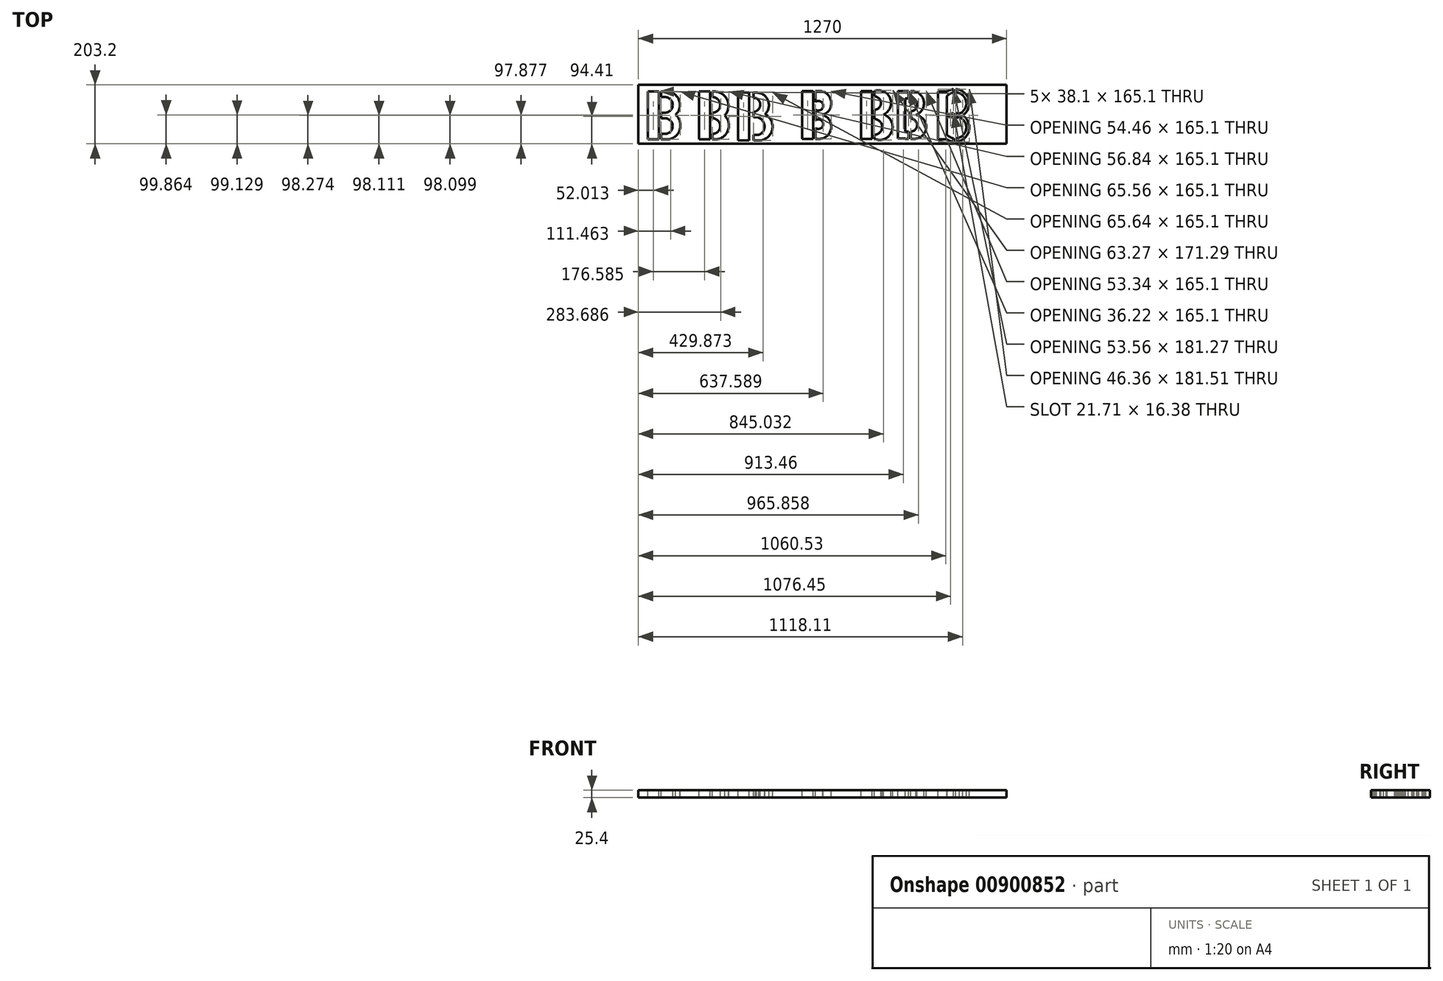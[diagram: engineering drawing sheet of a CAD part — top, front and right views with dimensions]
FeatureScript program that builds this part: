
annotation { "Feature Type Name" : "Feature", "Feature Type Description" : "" }
export const myFeature = defineFeature(function(context is Context, id is Id, definition is map)
    precondition{}
    {
        {
            var Q0;
            Q0=qCreatedBy(makeId("Top.planeOp"),FACE);
            var sketch = newSketch(context, id + "F0", { "sketchPlane" : qUnion([Q0])});
            skLineSegment(sketch, "E0.bottom", {"start": v(-873.94, -930.87) * mm, "end": v(396.06, -930.87) * mm});
            skLineSegment(sketch, "E0.top", {"start": v(-873.94, -1134.07) * mm, "end": v(396.06, -1134.07) * mm});
            skLineSegment(sketch, "E0.left", {"start": v(-873.94, -930.87) * mm, "end": v(-873.94, -1134.07) * mm});
            skLineSegment(sketch, "E0.right", {"start": v(396.06, -930.87) * mm, "end": v(396.06, -1134.07) * mm});
            skSolve(sketch);
        }
        {
            var Q0;
            Q0=makeQuery(id+"F0.imprint","IMPRINT",FACE,{"disambiguationData":[TD([[makeQuery(id+"F0.imprint","IMPRINT",EDGE,{"derivedFrom":sQuery(id+"F0.wireOp",EDGE,"E0.bottom")}),-1.0]])]});
            extrude(context, id + "F1", {"entities" : qUnion([Q0]), "depth" : 25.4 * mm, "offsetDistance" : 25.4 * mm});
        }
        {
            var Q0;
            Q0=makeQuery(id+"F1.opExtrude","CAP_FACE",FACE,{"disambiguationData":[OSD([sQuery(id+"F0.wireOp",EDGE,"E0.bottom"),sQuery(id+"F0.wireOp",EDGE,"E0.top"),sQuery(id+"F0.wireOp",EDGE,"E0.left"),sQuery(id+"F0.wireOp",EDGE,"E0.right")])],"isStart":false});
            var sketch = newSketch(context, id + "F2", { "sketchPlane" : qUnion([Q0])});
            skLineSegment(sketch, "E1.bottom", {"start": v(-840.98, -953.64) * mm, "end": v(-802.88, -953.64) * mm});
            skLineSegment(sketch, "E1.top", {"start": v(-840.98, -1118.74) * mm, "end": v(-802.88, -1118.74) * mm});
            skLineSegment(sketch, "E1.left", {"start": v(-840.98, -953.64) * mm, "end": v(-840.98, -1118.74) * mm});
            skLineSegment(sketch, "E1.right", {"start": v(-802.88, -953.64) * mm, "end": v(-802.88, -1118.74) * mm});
            skLineSegment(sketch, "E2", {"start": v(-795.26, -953.64) * mm, "end": v(-795.26, -1118.74) * mm});
            skLineSegment(sketch, "E3", {"start": v(-795.26, -953.64) * mm, "end": v(-776.2, -953.64) * mm});
            skPoint(sketch, "E3.endSnap0", {"position": v(-776.2, -1036.2) * mm});
            skLineSegment(sketch, "E4", {"start": v(-795.26, -1118.74) * mm, "end": v(-776.2, -1118.74) * mm});
            skLineSegment(sketch, "E5", {"start": v(-795.26, -1026.67) * mm, "end": v(-782.56, -1026.67) * mm});
            skLineSegment(sketch, "E6", {"start": v(-795.26, -1045.72) * mm, "end": v(-782.56, -1045.72) * mm});
            skLineSegment(sketch, "E7", {"start": v(-795.26, -1099.7) * mm, "end": v(-782.56, -1099.7) * mm});
            skArc(sketch, "E8", {"start": v(-782.56, -1099.7) * mm, "mid": v(-755.57, -1072.7) * mm, "end": v(-782.56, -1045.72) * mm});
            skLineSegment(sketch, "E9", {"start": v(-795.26, -972.7) * mm, "end": v(-782.56, -972.7) * mm});
            skArc(sketch, "E10", {"start": v(-782.56, -1026.67) * mm, "mid": v(-755.57, -999.68) * mm, "end": v(-782.56, -972.7) * mm});
            skLineSegment(sketch, "E11", {"start": v(-729.7, -1066.36) * mm, "end": v(-729.7, -1079.06) * mm});
            skPoint(sketch, "E12.orphan", {"position": v(-802.96, -1036.2) * mm});
            skLineSegment(sketch, "E13", {"start": v(-795.26, -1036.2) * mm, "end": v(-807.9, -1036.2) * mm});
            skLineSegment(sketch, "E14", {"start": v(-731.4, -993.33) * mm, "end": v(-731.4, -1006.03) * mm});
            skArc(sketch, "E15", {"start": v(-731.4, -993.33) * mm, "mid": v(-746.28, -965) * mm, "end": v(-776.2, -953.64) * mm});
            skArc(sketch, "E16", {"start": v(-729.7, -1066.36) * mm, "mid": v(-753.48, -1029.59) * mm, "end": v(-796.76, -1036.2) * mm});
            skArc(sketch, "E17", {"start": v(-776.2, -1118.74) * mm, "mid": v(-745.64, -1107.47) * mm, "end": v(-729.7, -1079.06) * mm});
            skArc(sketch, "E18.trimOffspring", {"start": v(-796.76, -1036.2) * mm, "mid": v(-755.37, -1039.98) * mm, "end": v(-731.4, -1006.03) * mm});
            skSolve(sketch);
        }
        {
            var Q0;
            Q0=makeQuery(id+"F2.imprint","IMPRINT",FACE,{"disambiguationData":[TD([[makeQuery(id+"F2.imprint","IMPRINT",EDGE,{"derivedFrom":sQuery(id+"F2.wireOp",EDGE,"E1.bottom")}),-1.0]])]});
            var Q1;
            {var subQ0=sQuery(id+"F2.wireOp",EDGE,"idpBYQ9l-Ms9j-yzLq-ZXLM-ZtzVa5Vgj7Lw");Q1=makeQuery(id+"F2.imprint","IMPRINT",FACE,{"disambiguationData":[TD([[makeQuery(id+"F2.imprint","IMPRINT",EDGE,{"derivedFrom":subQ0}),1.0]])]});}
            var Q2;
            {var subQ1=sQuery(id+"F2.wireOp",EDGE,"idpBYQ9l-Ms9j-yzLq-ZXLM-ZtzVa5Vgj7Lw");Q2=makeQuery(id+"F2.imprint","IMPRINT",FACE,{"disambiguationData":[TD([[makeQuery(id+"F2.imprint","IMPRINT",EDGE,{"derivedFrom":subQ1}),-1.0]])]});}
            var Q3;
            {var subQ5=sQuery(id+"F2.wireOp",EDGE,"E3");Q3=makeQuery(id+"F2.imprint","IMPRINT",FACE,{"disambiguationData":[TD([[makeQuery(id+"F2.imprint","IMPRINT",EDGE,{"derivedFrom":subQ5}),-1.0]])]});}
            var Q4;
            {var subQ1=sQuery(id+"F2.wireOp",EDGE,"E4");Q4=makeQuery(id+"F2.imprint","IMPRINT",FACE,{"disambiguationData":[TD([[makeQuery(id+"F2.imprint","IMPRINT",EDGE,{"derivedFrom":subQ1}),1.0]])]});}
            var Q5;
            {var subQ0=sQuery(id+"F2.wireOp",EDGE,"E2");var subQ1=makeQuery(id+"F2.imprint","INTERSECT",VERTEX,{"derivedFrom":[subQ0,sQuery(id+"F2.wireOp",EDGE,"E13")]});Q5=makeQuery(id+"F2.imprint","IMPRINT",FACE,{"disambiguationData":[TD([[makeQuery(id+"F2.imprint","IMPRINT",EDGE,{"disambiguationData":[TD([[subQ1,1.0]])],"derivedFrom":subQ0}),1.0]])]});}
            extrude(context, id + "F3", {"entities" : qUnion([Q0, Q1, Q2, Q3, Q4, Q5]), "operationType" : NewBodyOperationType.REMOVE, "oppositeDirection" : true, "depth" : 25.4 * mm, "offsetDistance" : 25.4 * mm});
        }
        {
            var Q0;
            Q0=makeQuery(id+"F1.opExtrude","CAP_FACE",FACE,{"disambiguationData":[OSD([sQuery(id+"F0.wireOp",EDGE,"E0.bottom"),sQuery(id+"F0.wireOp",EDGE,"E0.top"),sQuery(id+"F0.wireOp",EDGE,"E0.left"),sQuery(id+"F0.wireOp",EDGE,"E0.right")])],"isStart":false});
            var sketch = newSketch(context, id + "F4", { "sketchPlane" : qUnion([Q0])});
            skLineSegment(sketch, "E19.bottom", {"start": v(-664.4, -953.64) * mm, "end": v(-626.3, -953.64) * mm});
            skLineSegment(sketch, "E19.top", {"start": v(-664.4, -1118.74) * mm, "end": v(-626.3, -1118.74) * mm});
            skLineSegment(sketch, "E19.left", {"start": v(-664.4, -953.64) * mm, "end": v(-664.4, -1118.74) * mm});
            skLineSegment(sketch, "E19.right", {"start": v(-626.3, -953.64) * mm, "end": v(-626.3, -1118.74) * mm});
            skLineSegment(sketch, "E20", {"start": v(-661.28, -1036.2) * mm, "end": v(-576.47, -1036.2) * mm});
            skLineSegment(sketch, "E21", {"start": v(-618.67, -953.64) * mm, "end": v(-618.67, -1118.74) * mm});
            skLineSegment(sketch, "E22", {"start": v(-618.67, -953.64) * mm, "end": v(-612.21, -953.64) * mm});
            skLineSegment(sketch, "E23", {"start": v(-618.67, -972.7) * mm, "end": v(-610.9, -972.7) * mm});
            skLineSegment(sketch, "E24", {"start": v(-618.67, -1026.67) * mm, "end": v(-596.99, -1026.67) * mm});
            skLineSegment(sketch, "E25", {"start": v(-618.67, -1045.72) * mm, "end": v(-598.32, -1045.72) * mm});
            skLineSegment(sketch, "E26", {"start": v(-618.67, -1118.74) * mm, "end": v(-609.58, -1118.74) * mm});
            skLineSegment(sketch, "E27", {"start": v(-618.67, -1099.7) * mm, "end": v(-610.24, -1099.7) * mm});
            skArc(sketch, "E28", {"start": v(-618.67, -1026.67) * mm, "mid": v(-591.69, -999.68) * mm, "end": v(-618.67, -972.7) * mm});
            skArc(sketch, "E29", {"start": v(-618.67, -1099.7) * mm, "mid": v(-591.69, -1072.7) * mm, "end": v(-618.67, -1045.72) * mm});
            skArc(sketch, "E30", {"start": v(-609.58, -1118.74) * mm, "mid": v(-565.11, -1088.67) * mm, "end": v(-576.47, -1036.2) * mm});
            skArc(sketch, "E31", {"start": v(-576.47, -1036.2) * mm, "mid": v(-567.23, -983.18) * mm, "end": v(-612.21, -953.64) * mm});
            skSolve(sketch);
        }
        {
            var Q0;
            {var subQ1=sQuery(id+"F4.wireOp",EDGE,"E19.bottom");Q0=makeQuery(id+"F4.imprint","IMPRINT",FACE,{"disambiguationData":[TD([[makeQuery(id+"F4.imprint","IMPRINT",EDGE,{"derivedFrom":subQ1}),-1.0]])]});}
            var Q1;
            {var subQ0=sQuery(id+"F4.wireOp",EDGE,"E22");Q1=makeQuery(id+"F4.imprint","IMPRINT",FACE,{"disambiguationData":[TD([[makeQuery(id+"F4.imprint","IMPRINT",EDGE,{"derivedFrom":subQ0}),-1.0]])]});}
            var Q2;
            {var subQ0=sQuery(id+"F4.wireOp",EDGE,"E26");Q2=makeQuery(id+"F4.imprint","IMPRINT",FACE,{"disambiguationData":[TD([[makeQuery(id+"F4.imprint","IMPRINT",EDGE,{"derivedFrom":subQ0}),1.0]])]});}
            extrude(context, id + "F5", {"entities" : qUnion([Q0, Q1, Q2]), "operationType" : NewBodyOperationType.REMOVE, "oppositeDirection" : true, "depth" : 25.4 * mm, "offsetDistance" : 25.4 * mm});
        }
        {
            var Q0;
            Q0=makeQuery(id+"F1.opExtrude","CAP_FACE",FACE,{"disambiguationData":[OSD([sQuery(id+"F0.wireOp",EDGE,"E0.bottom"),sQuery(id+"F0.wireOp",EDGE,"E0.top"),sQuery(id+"F0.wireOp",EDGE,"E0.left"),sQuery(id+"F0.wireOp",EDGE,"E0.right")])],"isStart":false});
            var sketch = newSketch(context, id + "F6", { "sketchPlane" : qUnion([Q0])});
            skLineSegment(sketch, "E32.bottom", {"start": v(-309.3, -951.66) * mm, "end": v(-271.2, -951.66) * mm});
            skLineSegment(sketch, "E32.top", {"start": v(-309.3, -1116.76) * mm, "end": v(-271.2, -1116.76) * mm});
            skLineSegment(sketch, "E32.left", {"start": v(-309.3, -951.66) * mm, "end": v(-309.3, -1116.76) * mm});
            skLineSegment(sketch, "E32.right", {"start": v(-271.2, -951.66) * mm, "end": v(-271.2, -1116.76) * mm});
            skLineSegment(sketch, "E33", {"start": v(-263.58, -951.66) * mm, "end": v(-263.58, -1116.76) * mm});
            skLineSegment(sketch, "E34", {"start": v(-263.58, -951.66) * mm, "end": v(-250.88, -951.66) * mm});
            skLineSegment(sketch, "E35", {"start": v(-263.58, -1034.2) * mm, "end": v(-238.18, -1034.2) * mm});
            skLineSegment(sketch, "E36", {"start": v(-263.58, -1116.76) * mm, "end": v(-250.88, -1116.76) * mm});
            skLineSegment(sketch, "E37", {"start": v(-263.58, -1015.16) * mm, "end": v(-234.08, -1015.16) * mm});
            skLineSegment(sketch, "E38", {"start": v(-263.58, -1053.26) * mm, "end": v(-237.49, -1053.26) * mm});
            skLineSegment(sketch, "E39", {"start": v(-263.58, -989.76) * mm, "end": v(-228.48, -989.76) * mm});
            skLineSegment(sketch, "E40", {"start": v(-263.58, -1078.66) * mm, "end": v(-221.73, -1078.66) * mm});
            skArc(sketch, "E41", {"start": v(-263.58, -1015.16) * mm, "mid": v(-236.52, -1002.46) * mm, "end": v(-263.58, -989.76) * mm});
            skArc(sketch, "E42", {"start": v(-263.58, -1078.66) * mm, "mid": v(-236.52, -1065.96) * mm, "end": v(-263.58, -1053.26) * mm});
            skArc(sketch, "E43", {"start": v(-238.18, -1034.2) * mm, "mid": v(-209.12, -987.48) * mm, "end": v(-250.88, -951.66) * mm});
            skArc(sketch, "E44", {"start": v(-250.88, -1116.76) * mm, "mid": v(-209.12, -1080.93) * mm, "end": v(-238.18, -1034.2) * mm});
            skSolve(sketch);
        }
        {
            var Q0;
            Q0=makeQuery(id+"F6.imprint","IMPRINT",FACE,{"disambiguationData":[TD([[makeQuery(id+"F6.imprint","IMPRINT",EDGE,{"derivedFrom":sQuery(id+"F6.wireOp",EDGE,"E32.bottom")}),-1.0]])]});
            var Q1;
            {var subQ0=sQuery(id+"F6.wireOp",EDGE,"E34");Q1=makeQuery(id+"F6.imprint","IMPRINT",FACE,{"disambiguationData":[TD([[makeQuery(id+"F6.imprint","IMPRINT",EDGE,{"derivedFrom":subQ0}),-1.0]])]});}
            var Q2;
            {var subQ0=sQuery(id+"F6.wireOp",EDGE,"E35");Q2=makeQuery(id+"F6.imprint","IMPRINT",FACE,{"disambiguationData":[TD([[makeQuery(id+"F6.imprint","IMPRINT",EDGE,{"derivedFrom":subQ0}),-1.0]])]});}
            extrude(context, id + "F7", {"entities" : qUnion([Q0, Q1, Q2]), "operationType" : NewBodyOperationType.REMOVE, "oppositeDirection" : true, "depth" : 25.4 * mm, "offsetDistance" : 25.4 * mm});
        }
        {
            var Q0;
            Q0=makeQuery(id+"F1.opExtrude","CAP_FACE",FACE,{"disambiguationData":[OSD([sQuery(id+"F0.wireOp",EDGE,"E0.bottom"),sQuery(id+"F0.wireOp",EDGE,"E0.top"),sQuery(id+"F0.wireOp",EDGE,"E0.left"),sQuery(id+"F0.wireOp",EDGE,"E0.right")])],"isStart":false});
            var sketch = newSketch(context, id + "F8", { "sketchPlane" : qUnion([Q0])});
            skLineSegment(sketch, "E45", {"start": v(-530.23, -957.11) * mm, "end": v(-530.23, -1122.21) * mm});
            skLineSegment(sketch, "E46", {"start": v(-530.23, -1122.21) * mm, "end": v(-492.13, -1122.21) * mm});
            skLineSegment(sketch, "E47", {"start": v(-492.13, -1122.21) * mm, "end": v(-492.13, -957.11) * mm});
            skLineSegment(sketch, "E48", {"start": v(-492.13, -957.11) * mm, "end": v(-530.23, -957.11) * mm});
            skLineSegment(sketch, "E49", {"start": v(-476.9, -1122.21) * mm, "end": v(-458.66, -1122.21) * mm});
            skLineSegment(sketch, "E50", {"start": v(-476.9, -1103.16) * mm, "end": v(-458.66, -1103.16) * mm});
            skLineSegment(sketch, "E51", {"start": v(-458.66, -1103.16) * mm, "end": v(-458.66, -1103.94) * mm});
            skLineSegment(sketch, "E52", {"start": v(-476.9, -1041.57) * mm, "end": v(-470.78, -1041.57) * mm});
            skLineSegment(sketch, "E53", {"start": v(-476.9, -1022.52) * mm, "end": v(-470.78, -1022.52) * mm});
            skLineSegment(sketch, "E54", {"start": v(-476.9, -957.11) * mm, "end": v(-467.16, -957.11) * mm});
            skLineSegment(sketch, "E55", {"start": v(-476.9, -976.16) * mm, "end": v(-467.16, -976.16) * mm});
            skArc(sketch, "E56", {"start": v(-470.78, -1022.52) * mm, "mid": v(-453.83, -1000.52) * mm, "end": v(-467.16, -976.16) * mm});
            skArc(sketch, "E57", {"start": v(-437.13, -1032.04) * mm, "mid": v(-426.8, -984.42) * mm, "end": v(-467.16, -957.11) * mm});
            skArc(sketch, "E58", {"start": v(-458.66, -1122.21) * mm, "mid": v(-412.31, -1085.62) * mm, "end": v(-437.13, -1032.04) * mm});
            skArc(sketch, "E59", {"start": v(-458.66, -1103.16) * mm, "mid": v(-439.4, -1067.38) * mm, "end": v(-470.78, -1041.57) * mm});
            skLineSegment(sketch, "E60", {"start": v(-476.9, -957.11) * mm, "end": v(-476.9, -1122.21) * mm});
            skSolve(sketch);
        }
        {
            var Q0;
            Q0=makeQuery(id+"F8.imprint","IMPRINT",FACE,{"disambiguationData":[TD([[makeQuery(id+"F8.imprint","IMPRINT",EDGE,{"derivedFrom":sQuery(id+"F8.wireOp",EDGE,"E45")}),1.0]])]});
            var Q1;
            {var subQ2=sQuery(id+"F8.wireOp",EDGE,"E49");Q1=makeQuery(id+"F8.imprint","IMPRINT",FACE,{"disambiguationData":[TD([[makeQuery(id+"F8.imprint","IMPRINT",EDGE,{"derivedFrom":subQ2}),1.0]])]});}
            extrude(context, id + "F9", {"entities" : qUnion([Q0, Q1]), "operationType" : NewBodyOperationType.REMOVE, "oppositeDirection" : true, "depth" : 25.4 * mm, "offsetDistance" : 25.4 * mm});
        }
        {
            var Q0;
            Q0=makeQuery(id+"F1.opExtrude","CAP_FACE",FACE,{"disambiguationData":[OSD([sQuery(id+"F0.wireOp",EDGE,"E0.bottom"),sQuery(id+"F0.wireOp",EDGE,"E0.top"),sQuery(id+"F0.wireOp",EDGE,"E0.left"),sQuery(id+"F0.wireOp",EDGE,"E0.right")])],"isStart":false});
            var sketch = newSketch(context, id + "F10", { "sketchPlane" : qUnion([Q0])});
            skLineSegment(sketch, "E61", {"start": v(-60.54, -951.66) * mm, "end": v(-60.54, -1116.76) * mm});
            skPoint(sketch, "E61.endSnap0", {"position": v(-290.25, -1116.76) * mm});
            skArc(sketch, "E62", {"start": v(-28.11, -1032.68) * mm, "mid": v(-5.68, -976.7) * mm, "end": v(-60.54, -951.66) * mm});
            skArc(sketch, "E63", {"start": v(-60.54, -1116.76) * mm, "mid": v(-0.26, -1091.71) * mm, "end": v(-28.11, -1032.68) * mm});
            skArc(sketch, "E64", {"start": v(-60.54, -1016.52) * mm, "mid": v(-37.36, -993.33) * mm, "end": v(-60.54, -970.14) * mm});
            skArc(sketch, "E65", {"start": v(-60.54, -1102.78) * mm, "mid": v(-33.24, -1075.48) * mm, "end": v(-60.54, -1048.18) * mm});
            skPoint(sketch, "E66.orphan", {"position": v(-60.54, -1034.2) * mm});
            skLineSegment(sketch, "E67.bottom", {"start": v(-106.26, -951.66) * mm, "end": v(-68.16, -951.66) * mm});
            skLineSegment(sketch, "E67.top", {"start": v(-106.26, -1116.76) * mm, "end": v(-68.16, -1116.76) * mm});
            skLineSegment(sketch, "E67.left", {"start": v(-106.26, -951.66) * mm, "end": v(-106.26, -1116.76) * mm});
            skLineSegment(sketch, "E67.right", {"start": v(-68.16, -951.66) * mm, "end": v(-68.16, -1116.76) * mm});
            skSolve(sketch);
        }
        {
            var Q0;
            {var subQ4=sQuery(id+"F10.wireOp",EDGE,"E62");Q0=makeQuery(id+"F10.imprint","IMPRINT",FACE,{"disambiguationData":[TD([[makeQuery(id+"F10.imprint","IMPRINT",EDGE,{"derivedFrom":subQ4}),1.0]])]});}
            var Q1;
            Q1=makeQuery(id+"F10.imprint","IMPRINT",FACE,{"disambiguationData":[TD([[makeQuery(id+"F10.imprint","IMPRINT",EDGE,{"derivedFrom":sQuery(id+"F10.wireOp",EDGE,"E67.bottom")}),-1.0]])]});
            extrude(context, id + "F11", {"entities" : qUnion([Q0, Q1]), "operationType" : NewBodyOperationType.REMOVE, "oppositeDirection" : true, "depth" : 25.4 * mm, "offsetDistance" : 25.4 * mm});
        }
        {
            var Q0;
            Q0=makeQuery(id+"F1.opExtrude","CAP_FACE",FACE,{"disambiguationData":[OSD([sQuery(id+"F0.wireOp",EDGE,"E0.bottom"),sQuery(id+"F0.wireOp",EDGE,"E0.top"),sQuery(id+"F0.wireOp",EDGE,"E0.left"),sQuery(id+"F0.wireOp",EDGE,"E0.right")])],"isStart":false});
            var sketch = newSketch(context, id + "F12", { "sketchPlane" : qUnion([Q0])});
            skLineSegment(sketch, "E68", {"start": v(46.81, -951.66) * mm, "end": v(46.81, -1116.76) * mm});
            skLineSegment(sketch, "E69", {"start": v(46.81, -1116.76) * mm, "end": v(57.63, -1116.76) * mm});
            skLineSegment(sketch, "E70", {"start": v(46.81, -951.66) * mm, "end": v(57.63, -951.66) * mm});
            skLineSegment(sketch, "E71", {"start": v(46.81, -1034.2) * mm, "end": v(57.63, -1034.2) * mm});
            skLineSegment(sketch, "E72", {"start": v(46.81, -977.06) * mm, "end": v(57.63, -977.06) * mm});
            skLineSegment(sketch, "E73", {"start": v(46.81, -1021.5) * mm, "end": v(57.63, -1021.5) * mm});
            skLineSegment(sketch, "E74", {"start": v(46.81, -1046.9) * mm, "end": v(57.63, -1046.9) * mm});
            skLineSegment(sketch, "E75", {"start": v(46.81, -1091.36) * mm, "end": v(57.63, -1091.36) * mm});
            skArc(sketch, "E76", {"start": v(65.25, -1021.5) * mm, "mid": v(87.47, -999.28) * mm, "end": v(65.25, -977.06) * mm});
            skArc(sketch, "E77", {"start": v(65.25, -1091.36) * mm, "mid": v(87.47, -1069.13) * mm, "end": v(65.25, -1046.9) * mm});
            skLineSegment(sketch, "E78.bottom", {"start": v(46.81, -951.66) * mm, "end": v(21.41, -951.66) * mm});
            skLineSegment(sketch, "E78.top", {"start": v(46.81, -1116.28) * mm, "end": v(21.41, -1116.28) * mm});
            skLineSegment(sketch, "E78.left", {"start": v(46.81, -951.66) * mm, "end": v(46.81, -1116.28) * mm});
            skLineSegment(sketch, "E78.right", {"start": v(21.41, -951.66) * mm, "end": v(21.41, -1116.28) * mm});
            skArc(sketch, "E79", {"start": v(83.54, -1034.2) * mm, "mid": v(110.4, -986.64) * mm, "end": v(68.45, -951.66) * mm});
            skArc(sketch, "E80", {"start": v(77.2, -1116.76) * mm, "mid": v(118.59, -1078.42) * mm, "end": v(83.54, -1034.2) * mm});
            skLineSegment(sketch, "E81.left", {"start": v(57.63, -951.66) * mm, "end": v(57.63, -1116.76) * mm});
            skLineSegment(sketch, "E81.right", {"start": v(65.25, -951.66) * mm, "end": v(65.25, -1116.76) * mm});
            skLineSegment(sketch, "E82.trimOffspring", {"start": v(65.25, -951.66) * mm, "end": v(68.45, -951.66) * mm});
            skLineSegment(sketch, "E83.trimOffspring", {"start": v(65.25, -1034.2) * mm, "end": v(83.54, -1034.2) * mm});
            skLineSegment(sketch, "E84.trimOffspring", {"start": v(65.25, -1116.76) * mm, "end": v(77.2, -1116.76) * mm});
            skPoint(sketch, "E81.top.end.orphan", {"position": v(65.25, -1125.77) * mm});
            skSolve(sketch);
        }
        {
            var Q0;
            {var subQ3=sQuery(id+"F12.wireOp",EDGE,"E78.bottom");Q0=makeQuery(id+"F12.imprint","IMPRINT",FACE,{"disambiguationData":[TD([[makeQuery(id+"F12.imprint","IMPRINT",EDGE,{"derivedFrom":subQ3}),1.0]])]});}
            var Q1;
            {var subQ4=sQuery(id+"F12.wireOp",EDGE,"E70");Q1=makeQuery(id+"F12.imprint","IMPRINT",FACE,{"disambiguationData":[TD([[makeQuery(id+"F12.imprint","IMPRINT",EDGE,{"derivedFrom":subQ4}),-1.0]])]});}
            var Q2;
            {var subQ3=sQuery(id+"F12.wireOp",EDGE,"E68");Q2=makeQuery(id+"F12.imprint","IMPRINT",FACE,{"disambiguationData":[TD([[makeQuery(id+"F12.imprint","IMPRINT",EDGE,{"derivedFrom":subQ3}),1.0]])]});}
            var Q3;
            {var subQ1=sQuery(id+"F12.wireOp",EDGE,"E76");Q3=makeQuery(id+"F12.imprint","IMPRINT",FACE,{"disambiguationData":[TD([[makeQuery(id+"F12.imprint","IMPRINT",EDGE,{"derivedFrom":subQ1}),-1.0]])]});}
            var Q4;
            {var subQ1=sQuery(id+"F12.wireOp",EDGE,"E77");Q4=makeQuery(id+"F12.imprint","IMPRINT",FACE,{"disambiguationData":[TD([[makeQuery(id+"F12.imprint","IMPRINT",EDGE,{"derivedFrom":subQ1}),-1.0]])]});}
            extrude(context, id + "F13", {"entities" : qUnion([Q0, Q1, Q2, Q3, Q4]), "operationType" : NewBodyOperationType.REMOVE, "oppositeDirection" : true, "depth" : 25.4 * mm, "offsetDistance" : 25.4 * mm});
        }
        {
            var Q0;
            Q0=makeQuery(id+"F1.opExtrude","CAP_FACE",FACE,{"disambiguationData":[OSD([sQuery(id+"F0.wireOp",EDGE,"E0.bottom"),sQuery(id+"F0.wireOp",EDGE,"E0.top"),sQuery(id+"F0.wireOp",EDGE,"E0.left"),sQuery(id+"F0.wireOp",EDGE,"E0.right")])],"isStart":false});
            var sketch = newSketch(context, id + "F14", { "sketchPlane" : qUnion([Q0])});
            skArc(sketch, "E85", {"start": v(191.66, -1036.74) * mm, "mid": v(202.1, -1041.64) * mm, "end": v(213.37, -1043.99) * mm});
            skArc(sketch, "E86", {"start": v(190.37, -1118.46) * mm, "mid": v(201.36, -1123.97) * mm, "end": v(213.37, -1126.6) * mm});
            skArc(sketch, "E87", {"start": v(233.03, -1029.97) * mm, "mid": v(256.36, -988.47) * mm, "end": v(221, -956.6) * mm});
            skArc(sketch, "E88", {"start": v(190.37, -1102.59) * mm, "mid": v(200.77, -1110.82) * mm, "end": v(213.37, -1114.99) * mm});
            skLineSegment(sketch, "E89", {"start": v(190.37, -953.36) * mm, "end": v(159.82, -953.36) * mm});
            skLineSegment(sketch, "E90", {"start": v(159.82, -953.36) * mm, "end": v(159.82, -1118.35) * mm});
            skLineSegment(sketch, "E91", {"start": v(159.82, -1118.35) * mm, "end": v(190.37, -1118.46) * mm});
            skPoint(sketch, "E92.orphan", {"position": v(190.37, -1020.04) * mm});
            skPoint(sketch, "E93.trimOffspring.end.orphan", {"position": v(190.37, -1051.79) * mm});
            skArc(sketch, "E94.trimOffspring", {"start": v(245.14, -1035.93) * mm, "mid": v(265.64, -981.9) * mm, "end": v(221, -945.2) * mm});
            skLineSegment(sketch, "E95", {"start": v(212.92, -945.34) * mm, "end": v(213.37, -962.59) * mm});
            skLineSegment(sketch, "E96", {"start": v(213.37, -962.59) * mm, "end": v(213.37, -1126.6) * mm});
            skLineSegment(sketch, "E97", {"start": v(221, -1126.71) * mm, "end": v(221, -945.2) * mm});
            skArc(sketch, "E98.trimOffspring", {"start": v(212.92, -945.34) * mm, "mid": v(201.15, -947.97) * mm, "end": v(190.37, -953.36) * mm});
            skArc(sketch, "E99.trimOffspring", {"start": v(213.22, -956.95) * mm, "mid": v(200.72, -961.09) * mm, "end": v(190.37, -969.24) * mm});
            skArc(sketch, "E100.trimOffspring", {"start": v(221, -1044.08) * mm, "mid": v(226.97, -1043.32) * mm, "end": v(232.82, -1041.84) * mm});
            skArc(sketch, "E101.trimOffspring", {"start": v(221, -1115.32) * mm, "mid": v(256.46, -1083.34) * mm, "end": v(232.82, -1041.84) * mm});
            skArc(sketch, "E102.trimOffspring", {"start": v(221, -1126.71) * mm, "mid": v(265.75, -1090.02) * mm, "end": v(245.14, -1035.93) * mm});
            skArc(sketch, "E103", {"start": v(233.03, -1029.97) * mm, "mid": v(223.32, -1027.8) * mm, "end": v(213.37, -1027.6) * mm});
            skArc(sketch, "E104", {"start": v(213.37, -1027.6) * mm, "mid": v(202.07, -1030.05) * mm, "end": v(191.66, -1035.06) * mm});
            skLineSegment(sketch, "E105", {"start": v(190.37, -969.24) * mm, "end": v(190.37, -1102.59) * mm});
            skLineSegment(sketch, "E106", {"start": v(191.66, -1035.06) * mm, "end": v(191.66, -1036.74) * mm});
            skPoint(sketch, "E107.orphan", {"position": v(190.37, -1035.91) * mm});
            skSolve(sketch);
        }
        {
            var Q0;
            {var subQ5=sQuery(id+"F14.wireOp",EDGE,"E89");Q0=makeQuery(id+"F14.imprint","IMPRINT",FACE,{"disambiguationData":[TD([[makeQuery(id+"F14.imprint","IMPRINT",EDGE,{"derivedFrom":subQ5}),1.0]])]});}
            var Q1;
            {var subQ0=sQuery(id+"F14.wireOp",EDGE,"E98.trimOffspring");Q1=makeQuery(id+"F14.imprint","IMPRINT",FACE,{"disambiguationData":[TD([[makeQuery(id+"F14.imprint","IMPRINT",EDGE,{"derivedFrom":subQ0}),1.0]])]});}
            var Q2;
            {var subQ6=sQuery(id+"F14.wireOp",EDGE,"E87");Q2=makeQuery(id+"F14.imprint","IMPRINT",FACE,{"disambiguationData":[TD([[makeQuery(id+"F14.imprint","IMPRINT",EDGE,{"derivedFrom":subQ6}),-1.0]])]});}
            var Q3;
            {var subQ0=sQuery(id+"F14.wireOp",EDGE,"E85");Q3=makeQuery(id+"F14.imprint","IMPRINT",FACE,{"disambiguationData":[TD([[makeQuery(id+"F14.imprint","IMPRINT",EDGE,{"derivedFrom":subQ0}),1.0]])]});}
            var Q4;
            {var subQ0=sQuery(id+"F14.wireOp",EDGE,"E86");Q4=makeQuery(id+"F14.imprint","IMPRINT",FACE,{"disambiguationData":[TD([[makeQuery(id+"F14.imprint","IMPRINT",EDGE,{"derivedFrom":subQ0}),1.0]])]});}
            var Q5;
            {var subQ2=sQuery(id+"F14.wireOp",EDGE,"47eeabeb-d094-4876-8b21-216e1809bdd7.trimOffspring");Q5=makeQuery(id+"F14.imprint","IMPRINT",FACE,{"disambiguationData":[TD([[makeQuery(id+"F14.imprint","IMPRINT",EDGE,{"derivedFrom":subQ2}),1.0]])]});}
            extrude(context, id + "F15", {"entities" : qUnion([Q0, Q1, Q2, Q3, Q4, Q5]), "operationType" : NewBodyOperationType.REMOVE, "oppositeDirection" : true, "depth" : 25.4 * mm, "offsetDistance" : 25.4 * mm});
        }
    });
